# Revit family: Sanitary_Wash-basins_DURAVIT-AG_D-Code-Vanity-basin-033849
name_source: partatom
category: Plumbing Fixtures
revit_build: Autodesk Revit 2018 (Build: 20190510_1515(x64)
units: mm (PartAtom-declared; Revit-internal decimal feet)

## family parameters
Cut with Voids When Loaded = No
Host = Face
OmniClass Number = 23.31.13.00
OmniClass Title = Sinks
Part Type = Normal
Room Calculation Point = No
Round Connector Dimension = Use Diameter
Shared = No

## types (1)
- D-Code Vanity basin - 033849
    BIMobject category = Wash basins
    Connector Description = Water outlet
    Default Elevation = 1219 mm
    Description = Duravit D-Code Vanity washbasin 495 mm White High Gloss, Number of faucet holes per wash area: 0, Overflow - 0338490000
    Design country = Germany
    Details material = Duravit - Metal - 10 - Chrome
    ETIM classification = EC011550 | Washbasin
    Edition number = 1
    IFC Classification = Sanitary Terminal
    Installation instructions = http://pro.duravit.com
    Main material = Duravit - Ceramic - 00 - White Alpin
    Manufacturer = Duravit
    Manufacturer name = DURAVIT AG
    Masterformat 2014 Code = 22 41 16.13
    Masterformat 2014 Description = Residential Lavatories
    Material main = Ceramics
    Model = D-Code Vanity basin - 033849
    OmniClass Code = 23-31 13 00
    OmniClass Description = Sinks
    Outlet Diameter = 32  [stored 0.104987 ft]
    Product Guid = 6b825862-409c-4e59-b63e-c6949578d2e1
    Product SKU = d-code-vanity-basin-033849
    Product certification = http://pro.duravit.com
    Product data url = https://bimobject.com
    Product family = D-Code
    Product group = Washbowl
    Product name = D-Code Vanity basin - 033849
    Product url = http://pro.duravit.com
    QR code = https://bimobject.com
    Technical description = http://pro.duravit.com
    UNSPSC Code = 30181504
    URL = https://www.duravit.com
    Uniclass 2015 Code = Pr_40_20_96
    Uniclass 2015 Name = Wash basins, sinks and troughs
    Uniformat II Code = D2010
    Uniformat II Description = Plumbing Fixtures
    Weight Net (Kg) = 10
    Youtube clip = http://pro.duravit.com

note: [stored X ft] marks values corroborated as IEEE doubles in the binary element streams (Revit-internal decimal feet)

## geometry (parser evidence)
native form markers: Sweep x2
no freeform markers — native parametric forms only
